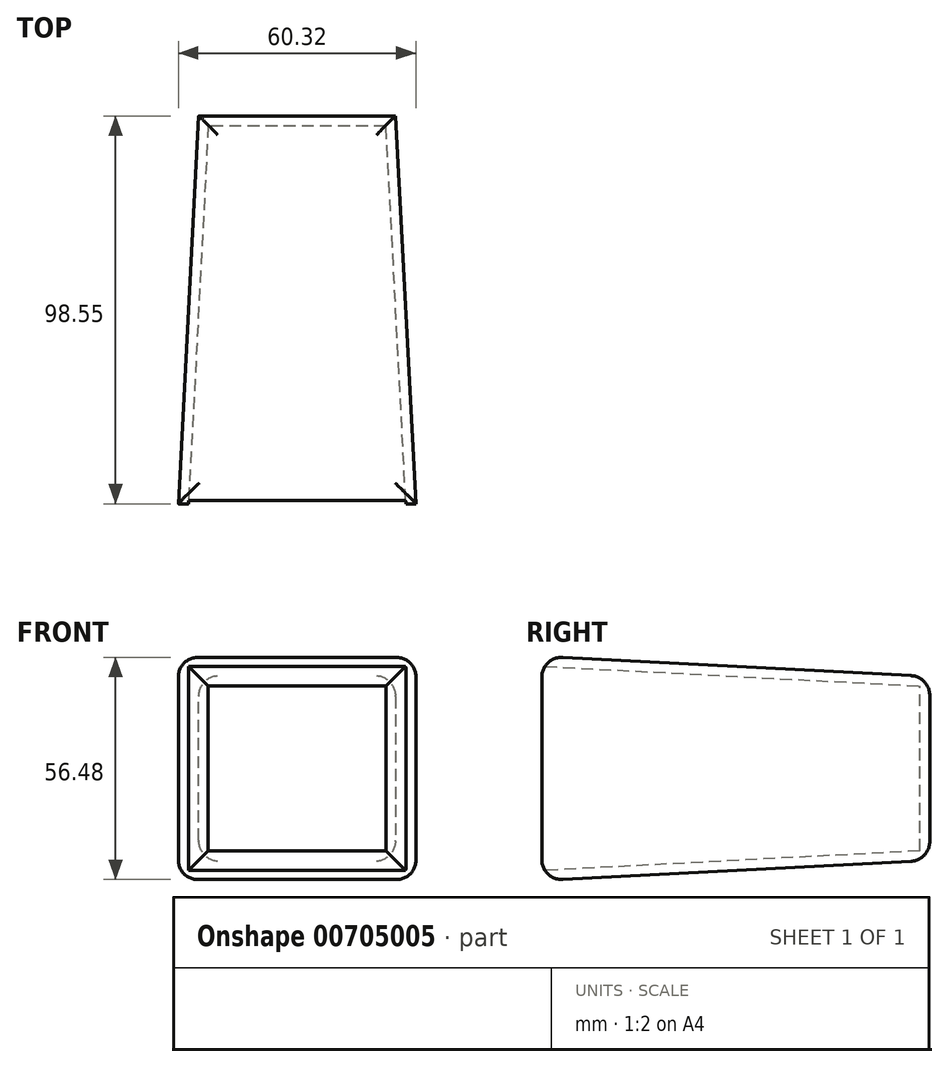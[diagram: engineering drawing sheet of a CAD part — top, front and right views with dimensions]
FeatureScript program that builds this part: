
annotation { "Feature Type Name" : "Feature", "Feature Type Description" : "" }
export const myFeature = defineFeature(function(context is Context, id is Id, definition is map)
    precondition{}
    {
        {
            var Q0;
            Q0=qCreatedBy(makeId("Front.planeOp"),FACE);
            var sketch = newSketch(context, id + "F0", { "sketchPlane" : qUnion([Q0])});
            skLineSegment(sketch, "E0.bottom", {"start": v(-25, -23.35) * mm, "end": v(25, -23.35) * mm});
            skLineSegment(sketch, "E0.top", {"start": v(-25, 23.35) * mm, "end": v(25, 23.35) * mm});
            skLineSegment(sketch, "E0.left", {"start": v(-25, -23.35) * mm, "end": v(-25, 23.35) * mm});
            skLineSegment(sketch, "E0.right", {"start": v(25, -23.35) * mm, "end": v(25, 23.35) * mm});
            skPoint(sketch, "E0.middle", {"position": v(0, 0) * mm});
            skSolve(sketch);
        }
        {
            var Q0;
            Q0=makeQuery(id+"F0.imprint","IMPRINT",FACE,{"disambiguationData":[TD([[makeQuery(id+"F0.imprint","IMPRINT",EDGE,{"derivedFrom":sQuery(id+"F0.wireOp",EDGE,"E0.bottom")}),1.0]])]});
            extrude(context, id + "F1", {"entities" : qUnion([Q0]), "depth" : 98.55 * mm, "offsetDistance" : 25.4 * mm, "hasDraft" : true, "draftAngle" : 3 * degree});
        }
        {
            var Q0;
            Q0=makeQuery(id+"F1.opExtrude","CAP_FACE",FACE,{"disambiguationData":[OSD([sQuery(id+"F0.wireOp",EDGE,"E0.bottom"),sQuery(id+"F0.wireOp",EDGE,"E0.top"),sQuery(id+"F0.wireOp",EDGE,"E0.left"),sQuery(id+"F0.wireOp",EDGE,"E0.right")])],"isStart":false});
            shell(context, id + "F2", {"entities" : qUnion([Q0]), "thickness" : 2.54 * mm});
        }
        {
            var Q0;
            Q0=makeQuery(id+"F1.opExtrude","SWEPT_FACE",FACE,{"disambiguationData":[OSD([sQuery(id+"F0.wireOp",EDGE,"E0.top")])]});
            fillet(context, id + "F3", {"entities" : qUnion([Q0]), "radius" : 5.08 * mm, "tangentPropagation" : true, "allowEdgeOverflow" : false});
        }
        {
            var Q0;
            Q0=makeQuery(id+"F1.opExtrude","SWEPT_FACE",FACE,{"disambiguationData":[OSD([sQuery(id+"F0.wireOp",EDGE,"E0.bottom")])]});
            fillet(context, id + "F4", {"entities" : qUnion([Q0]), "radius" : 5.08 * mm, "tangentPropagation" : true, "allowEdgeOverflow" : false});
        }
    });
